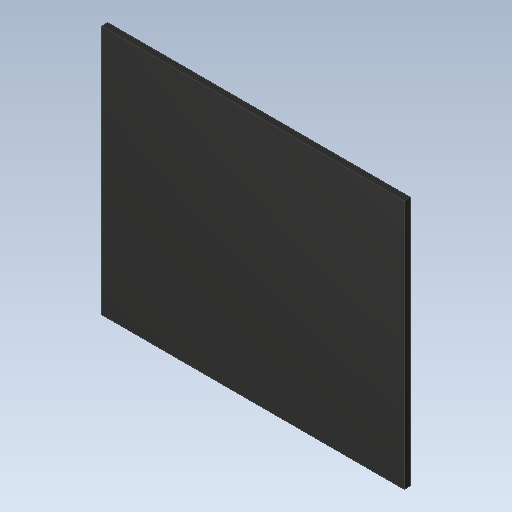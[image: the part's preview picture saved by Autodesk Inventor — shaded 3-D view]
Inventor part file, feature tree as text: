
AUTODESK INVENTOR PART (.ipt)
format: ipt  version: 2023 (Build 270158000, 158)  size: 92,672 bytes
history: imported  units: in
note: dims shown in document units (in); Inventor stores cm internally (conversion verified against a paired STEP export)
features: imported_body x1
ambient origin geometry x8: Origin, YZ Plane, XZ Plane, XY Plane, X Axis, Y Axis, Z Axis, Center Point
bodies: Solid1 (imported_parasolid), Body1 (imported_parasolid)
feature tree (1):
  imported_body  NMx_Import_Brep_tag  [imported B-rep: ~6 faces, bbox_mm=[5.0, 4.1303, 0.1]]
